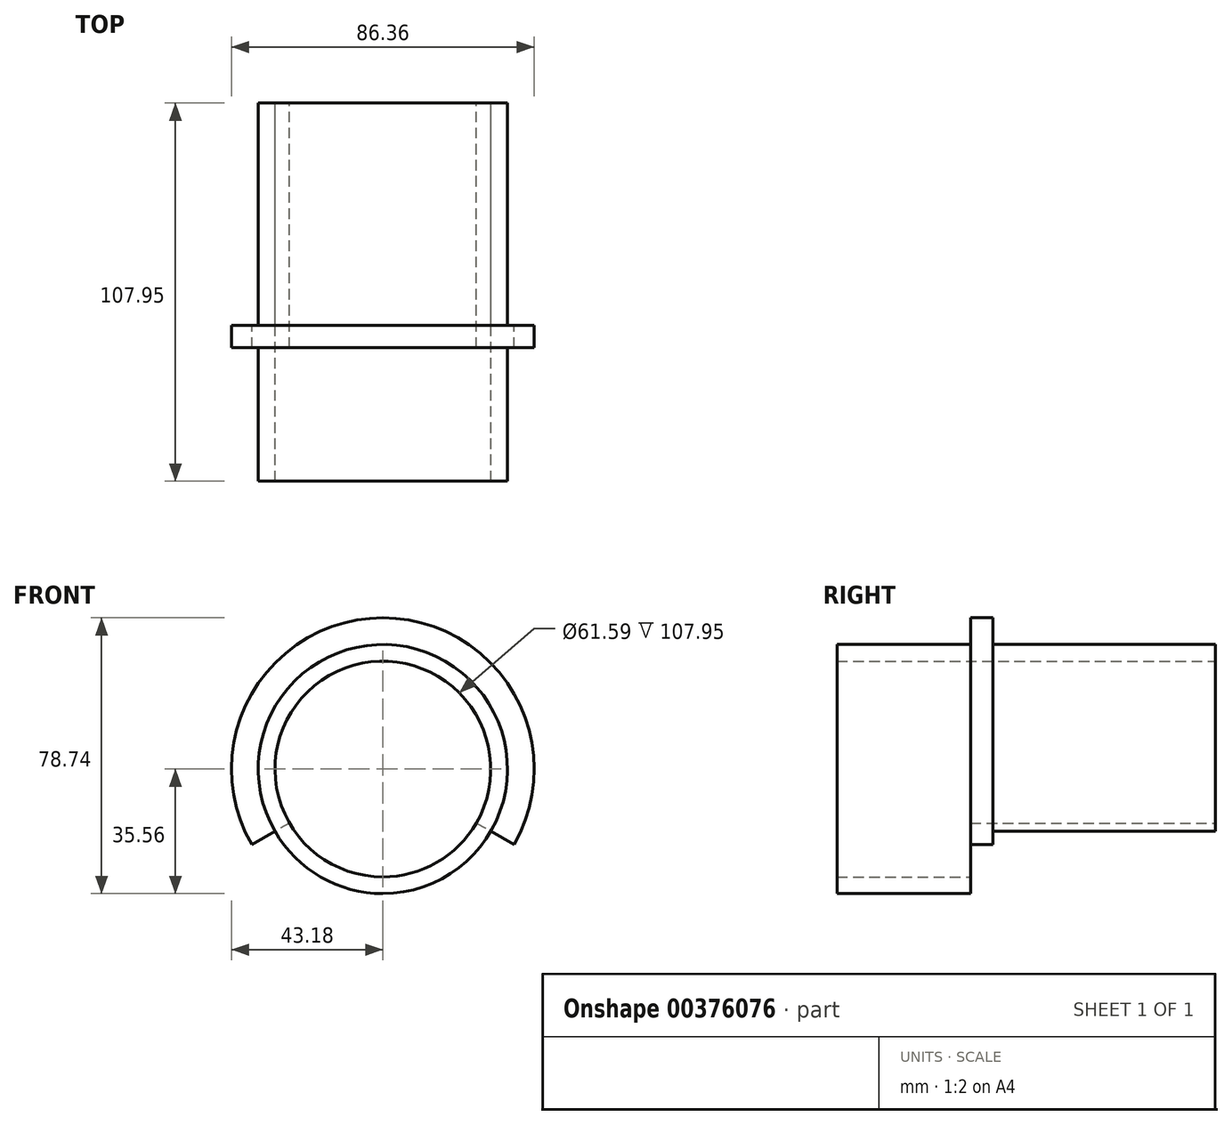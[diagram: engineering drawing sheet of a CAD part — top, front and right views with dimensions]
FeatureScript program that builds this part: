
annotation { "Feature Type Name" : "Feature", "Feature Type Description" : "" }
export const myFeature = defineFeature(function(context is Context, id is Id, definition is map)
    precondition{}
    {
        {
            var Q0;
            Q0=qCreatedBy(makeId("Front.planeOp"),FACE);
            var sketch = newSketch(context, id + "F0", { "sketchPlane" : qUnion([Q0])});
            skCircle(sketch, "E0", {"center": v(0, 0) * mm, "radius": 30.8 * mm});
            skCircle(sketch, "E1", {"center": v(0, 0) * mm, "radius": 35.56 * mm});
            skSolve(sketch);
        }
        {
            var Q0;
            Q0=makeQuery(id+"F0.imprint","IMPRINT",FACE,{"disambiguationData":[TD([[makeQuery(id+"F0.imprint","IMPRINT",EDGE,{"derivedFrom":sQuery(id+"F0.wireOp",EDGE,"E0")}),-1.0]])]});
            extrude(context, id + "F1", {"entities" : qUnion([Q0]), "depth" : 63.5 * mm});
        }
        {
            var Q0;
            Q0=makeQuery(id+"F1.opExtrude","CAP_FACE",FACE,{"disambiguationData":[OSD([sQuery(id+"F0.wireOp",EDGE,"E0"),sQuery(id+"F0.wireOp",EDGE,"E1")])],"isStart":false});
            var sketch = newSketch(context, id + "F2", { "sketchPlane" : qUnion([Q0])});
            skCircle(sketch, "E2", {"center": v(0, 0) * mm, "radius": 43.18 * mm});
            skSolve(sketch);
        }
        {
            var Q0;
            Q0=makeQuery(id+"F2.imprint","IMPRINT",FACE,{"disambiguationData":[TD([[makeQuery(id+"F2.imprint","IMPRINT",EDGE,{"derivedFrom":sQuery(id+"F2.wireOp",EDGE,"E2")}),1.0]])]});
            var Q1;
            Q1=makeQuery(id+"F2.imprint","IMPRINT",FACE,{"disambiguationData":[TD([[makeQuery(id+"F2.imprint","IMPRINT",EDGE,{"derivedFrom":makeQuery(id+"F1.opExtrude","CAP_EDGE",EDGE,{"disambiguationData":[OSD([sQuery(id+"F0.wireOp",EDGE,"E0")])],"isStart":false})}),-1.0]])]});
            extrude(context, id + "F3", {"entities" : qUnion([Q0, Q1]), "operationType" : NewBodyOperationType.ADD, "depth" : 6.35 * mm});
        }
        {
            var Q0;
            Q0=makeQuery(id+"F3.opExtrude","CAP_FACE",FACE,{"disambiguationData":[OSD([sQuery(id+"F0.wireOp",EDGE,"E0"),sQuery(id+"F2.wireOp",EDGE,"E2")])],"isStart":false});
            var sketch = newSketch(context, id + "F4", { "sketchPlane" : qUnion([Q0])});
            skCircle(sketch, "E3", {"center": v(0, 0) * mm, "radius": 35.56 * mm});
            skCircle(sketch, "E4", {"center": v(0, 0) * mm, "radius": 30.48 * mm});
            skSolve(sketch);
        }
        {
            var Q0;
            Q0=makeQuery(id+"F4.imprint","IMPRINT",FACE,{"disambiguationData":[TD([[makeQuery(id+"F4.imprint","IMPRINT",EDGE,{"derivedFrom":sQuery(id+"F4.wireOp",EDGE,"E3")}),1.0]])]});
            extrude(context, id + "F5", {"entities" : qUnion([Q0]), "operationType" : NewBodyOperationType.ADD, "depth" : 38.1 * mm});
        }
        {
            var Q0;
            Q0=makeQuery(id+"F1.opExtrude","CAP_FACE",FACE,{"disambiguationData":[OSD([sQuery(id+"F0.wireOp",EDGE,"E0"),sQuery(id+"F0.wireOp",EDGE,"E1")])],"isStart":true});
            var sketch = newSketch(context, id + "F6", { "sketchPlane" : qUnion([Q0])});
            skLineSegment(sketch, "E5", {"start": v(0, 0) * mm, "end": v(-66.82, -38.58) * mm});
            skLineSegment(sketch, "E6", {"start": v(0, 0) * mm, "end": v(66.82, -38.58) * mm});
            skLineSegment(sketch, "E7", {"start": v(-66.82, -38.58) * mm, "end": v(66.82, -38.58) * mm});
            skSolve(sketch);
        }
        {
            var Q0;
            {var subQ0=sQuery(id+"F6.wireOp",EDGE,"E6");var subQ1=sQuery(id+"F6.wireOp",EDGE,"E5");var subQ2=makeQuery(id+"F6.imprint","INTERSECT",VERTEX,{"derivedFrom":[subQ1,subQ0]});Q0=makeQuery(id+"F6.imprint","IMPRINT",FACE,{"disambiguationData":[TD([[makeQuery(id+"F6.imprint","IMPRINT",EDGE,{"disambiguationData":[TD([[subQ2,-1.0]])],"derivedFrom":subQ1}),1.0]])]});}
            var Q1;
            {var subQ0=sQuery(id+"F6.wireOp",EDGE,"E5");var subQ1=makeQuery(id+"F1.opExtrude","CAP_EDGE",EDGE,{"disambiguationData":[OSD([sQuery(id+"F0.wireOp",EDGE,"E1")])],"isStart":true});var subQ2=makeQuery(id+"F6.imprint","INTERSECT",VERTEX,{"derivedFrom":[subQ1,subQ0]});Q1=makeQuery(id+"F6.imprint","IMPRINT",FACE,{"disambiguationData":[TD([[makeQuery(id+"F6.imprint","IMPRINT",EDGE,{"disambiguationData":[TD([[subQ2,1.0]])],"derivedFrom":subQ0}),1.0]])]});}
            var Q2;
            {var subQ0=sQuery(id+"F6.wireOp",EDGE,"E7");Q2=makeQuery(id+"F6.imprint","IMPRINT",FACE,{"disambiguationData":[TD([[makeQuery(id+"F6.imprint","IMPRINT",EDGE,{"derivedFrom":subQ0}),1.0]])]});}
            var Q3;
            Q3=makeQuery(id+"F3.opExtrude","CAP_FACE",FACE,{"disambiguationData":[OSD([sQuery(id+"F0.wireOp",EDGE,"E0"),sQuery(id+"F2.wireOp",EDGE,"E2")])],"isStart":true});
            extrude(context, id + "F7", {"entities" : qUnion([Q0, Q1, Q2]), "operationType" : NewBodyOperationType.REMOVE, "endBound" : BoundingType.UP_TO_SURFACE, "oppositeDirection" : true, "endBoundEntityFace" : qUnion([Q3]), "depth" : 25.4 * mm});
        }
        {
            var Q0;
            {var subQ0=sQuery(id+"F2.wireOp",EDGE,"E2");var subQ1=sQuery(id+"F0.wireOp",EDGE,"E0");Q0=makeQuery(id+"F7.boolean.opBoolean","MERGE",FACE,{"derivedFrom":[makeQuery(id+"F3.opExtrude","CAP_FACE",FACE,{"disambiguationData":[OSD([subQ1,subQ0])],"isStart":true}),makeQuery(id+"F7.opExtrude","CAP_FACE",FACE,{"disambiguationData":[OSD([subQ1,subQ0])],"isStart":false})]});}
            var sketch = newSketch(context, id + "F8", { "sketchPlane" : qUnion([Q0])});
            skArc(sketch, "E8.0", {"start": v(26.67, -15.4) * mm, "mid": v(0, -30.8) * mm, "end": v(-26.67, -15.4) * mm});
            skArc(sketch, "E9.0", {"start": v(-37.4, -21.59) * mm, "mid": v(0, -43.18) * mm, "end": v(37.4, -21.59) * mm});
            skLineSegment(sketch, "E10.0", {"start": v(26.67, -15.4) * mm, "end": v(30.8, -17.78) * mm});
            skLineSegment(sketch, "E11", {"start": v(-26.67, -15.4) * mm, "end": v(-37.4, -21.6) * mm});
            skLineSegment(sketch, "E12", {"start": v(26.67, -15.4) * mm, "end": v(37.4, -21.59) * mm});
            skSolve(sketch);
        }
        {
            var Q0;
            {var subQ3=sQuery(id+"F8.wireOp",EDGE,"E8.0");Q0=makeQuery(id+"F8.imprint","IMPRINT",FACE,{"disambiguationData":[TD([[makeQuery(id+"F8.imprint","IMPRINT",EDGE,{"derivedFrom":subQ3}),1.0]])]});}
            var Q1;
            Q1=makeQuery(id+"F3.opExtrude","CAP_FACE",FACE,{"disambiguationData":[OSD([sQuery(id+"F0.wireOp",EDGE,"E0"),sQuery(id+"F2.wireOp",EDGE,"E2")])],"isStart":false});
            extrude(context, id + "F9", {"entities" : qUnion([Q0]), "operationType" : NewBodyOperationType.REMOVE, "endBound" : BoundingType.UP_TO_SURFACE, "oppositeDirection" : true, "endBoundEntityFace" : qUnion([Q1]), "depth" : 25.4 * mm});
        }
    });
